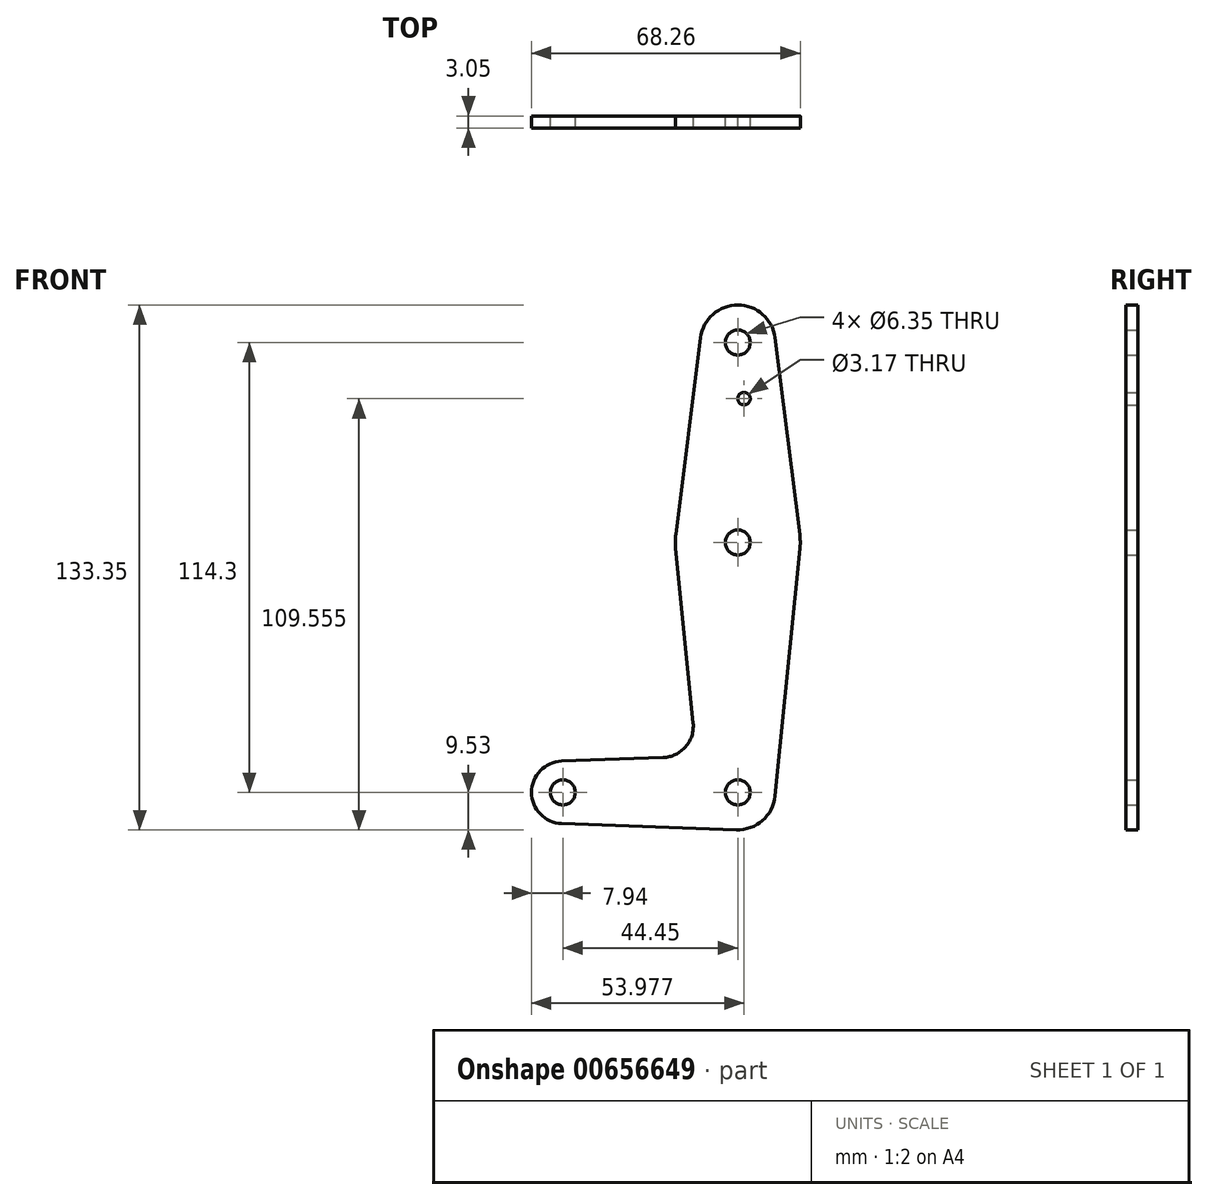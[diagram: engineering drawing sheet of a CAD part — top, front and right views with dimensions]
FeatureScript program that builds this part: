
annotation { "Feature Type Name" : "Feature", "Feature Type Description" : "" }
export const myFeature = defineFeature(function(context is Context, id is Id, definition is map)
    precondition{}
    {
        {
            var Q0;
            Q0=qCreatedBy(makeId("Front.planeOp"),FACE);
            var sketch = newSketch(context, id + "F0", { "sketchPlane" : qUnion([Q0])});
            skLineSegment(sketch, "E0", {"start": v(0, 0) * mm, "end": v(0, 50.8) * mm, "construction": true});
            skLineSegment(sketch, "E1", {"start": v(0, 0) * mm, "end": v(0, -63.5) * mm, "construction": true});
            skLineSegment(sketch, "E2", {"start": v(0, -63.5) * mm, "end": v(-44.45, -63.5) * mm, "construction": true});
            skCircle(sketch, "E3", {"center": v(0, 50.8) * mm, "radius": 9.53 * mm});
            skCircle(sketch, "E4", {"center": v(0, 0) * mm, "radius": 15.88 * mm});
            skCircle(sketch, "E5", {"center": v(0, -63.5) * mm, "radius": 9.53 * mm});
            skCircle(sketch, "E6", {"center": v(-44.45, -63.5) * mm, "radius": 7.94 * mm});
            skLineSegment(sketch, "E7", {"start": v(-9.45, 52) * mm, "end": v(-15.75, 1.98) * mm});
            skLineSegment(sketch, "E8", {"start": v(9.45, 52) * mm, "end": v(15.75, 1.98) * mm});
            skLineSegment(sketch, "E9", {"start": v(9.48, -64.45) * mm, "end": v(15.8, -1.59) * mm});
            skLineSegment(sketch, "E10", {"start": v(-15.8, -1.59) * mm, "end": v(-11.34, -45.9) * mm});
            skArc(sketch, "E11", {"start": v(-18.97, -54.65) * mm, "mid": v(-13.26, -51.93) * mm, "end": v(-11.34, -45.9) * mm});
            skLineSegment(sketch, "E12", {"start": v(-18.97, -54.65) * mm, "end": v(-44.73, -55.57) * mm});
            skLineSegment(sketch, "E13", {"start": v(-0.34, -73.02) * mm, "end": v(-44.73, -71.43) * mm});
            skCircle(sketch, "E14", {"center": v(0, 50.8) * mm, "radius": 3.18 * mm});
            skCircle(sketch, "E15", {"center": v(0, 0) * mm, "radius": 3.18 * mm});
            skCircle(sketch, "E16", {"center": v(0, -63.5) * mm, "radius": 3.18 * mm});
            skCircle(sketch, "E17", {"center": v(-44.45, -63.5) * mm, "radius": 3.18 * mm});
            skCircle(sketch, "E18", {"center": v(1.59, 36.53) * mm, "radius": 1.59 * mm});
            skSolve(sketch);
        }
        {
            var Q0;
            {var subQ0=sQuery(id+"F0.wireOp",EDGE,"E7");Q0=makeQuery(id+"F0.imprint","IMPRINT",FACE,{"disambiguationData":[TD([[makeQuery(id+"F0.imprint","IMPRINT",EDGE,{"derivedFrom":subQ0}),1.0]])]});}
            var Q1;
            Q1=makeQuery(id+"F0.imprint","IMPRINT",FACE,{"disambiguationData":[TD([[makeQuery(id+"F0.imprint","IMPRINT",EDGE,{"derivedFrom":sQuery(id+"F0.wireOp",EDGE,"E14")}),-1.0]])]});
            var Q2;
            Q2=makeQuery(id+"F0.imprint","IMPRINT",FACE,{"disambiguationData":[TD([[makeQuery(id+"F0.imprint","IMPRINT",EDGE,{"derivedFrom":sQuery(id+"F0.wireOp",EDGE,"E15")}),-1.0]])]});
            var Q3;
            Q3=makeQuery(id+"F0.imprint","IMPRINT",FACE,{"disambiguationData":[TD([[makeQuery(id+"F0.imprint","IMPRINT",EDGE,{"derivedFrom":sQuery(id+"F0.wireOp",EDGE,"E16")}),-1.0]])]});
            var Q4;
            {var subQ0=sQuery(id+"F0.wireOp",EDGE,"E9");Q4=makeQuery(id+"F0.imprint","IMPRINT",FACE,{"disambiguationData":[TD([[makeQuery(id+"F0.imprint","IMPRINT",EDGE,{"derivedFrom":subQ0}),1.0]])]});}
            var Q5;
            Q5=makeQuery(id+"F0.imprint","IMPRINT",FACE,{"disambiguationData":[TD([[makeQuery(id+"F0.imprint","IMPRINT",EDGE,{"derivedFrom":sQuery(id+"F0.wireOp",EDGE,"E17")}),-1.0]])]});
            extrude(context, id + "F1", {"entities" : qUnion([Q0, Q1, Q2, Q3, Q4, Q5]), "depth" : 3.05 * mm, "offsetDistance" : 25.4 * mm});
        }
    });
